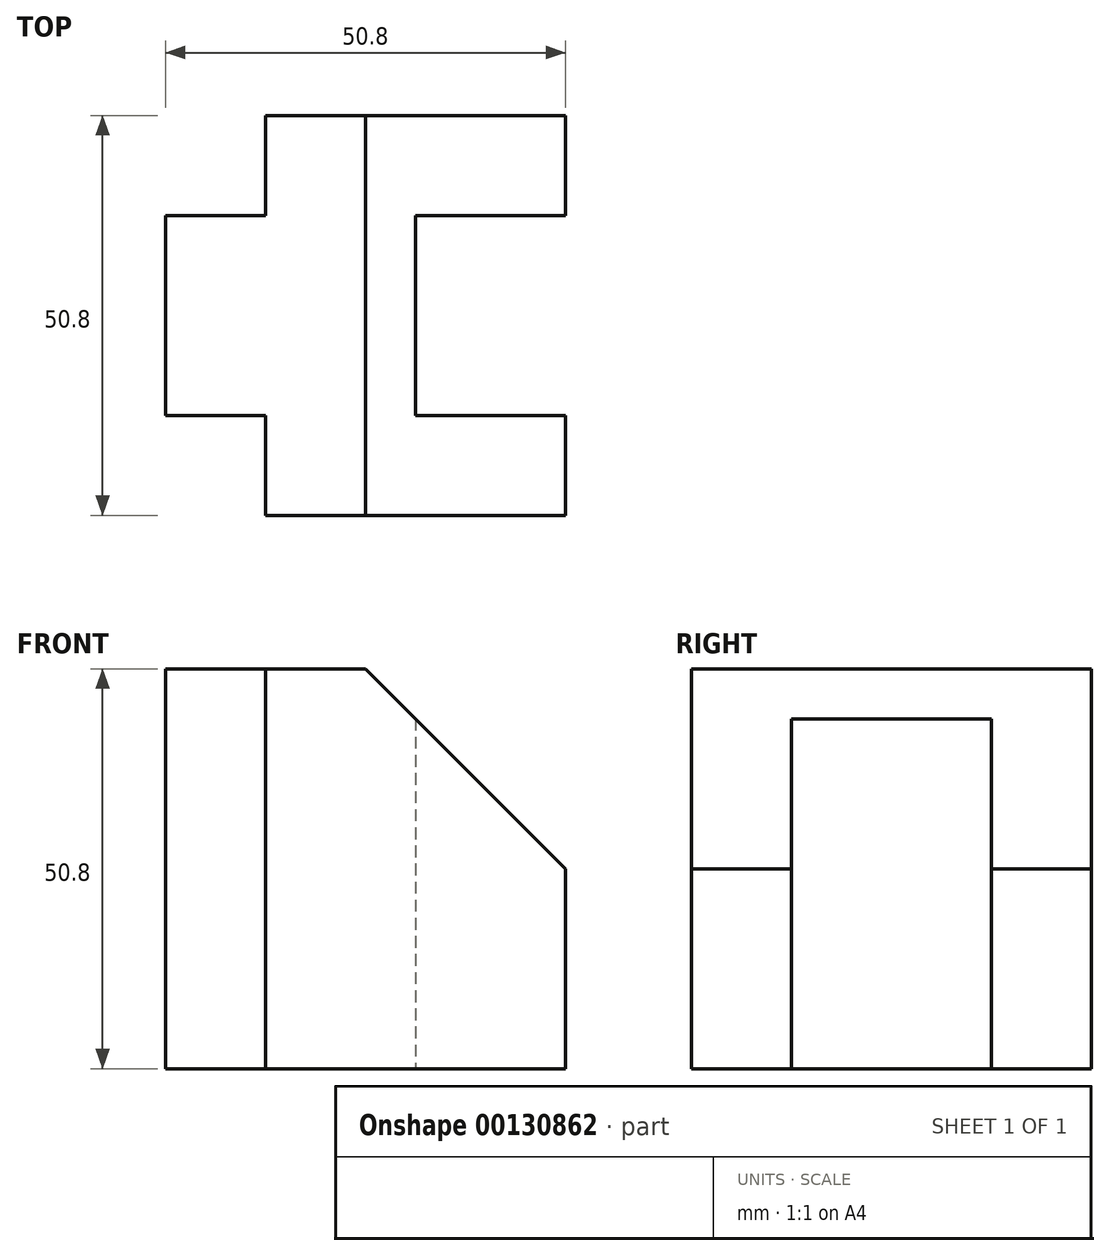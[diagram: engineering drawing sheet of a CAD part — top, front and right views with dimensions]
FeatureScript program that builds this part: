
annotation { "Feature Type Name" : "Feature", "Feature Type Description" : "" }
export const myFeature = defineFeature(function(context is Context, id is Id, definition is map)
    precondition{}
    {
        {
            var Q0;
            Q0=qCreatedBy(makeId("Front.planeOp"),FACE);
            var sketch = newSketch(context, id + "F0", { "sketchPlane" : qUnion([Q0])});
            skLineSegment(sketch, "E0.bottom", {"start": v(0, 0) * mm, "end": v(50.8, 0) * mm});
            skLineSegment(sketch, "E0.top", {"start": v(0, 50.8) * mm, "end": v(25.4, 50.8) * mm});
            skLineSegment(sketch, "E0.left", {"start": v(0, 0) * mm, "end": v(0, 50.8) * mm});
            skLineSegment(sketch, "E0.right", {"start": v(50.8, 0) * mm, "end": v(50.8, 25.4) * mm});
            skLineSegment(sketch, "E1", {"start": v(50.8, 25.4) * mm, "end": v(25.4, 50.8) * mm});
            skLineSegment(sketch, "E2", {"start": v(50.8, 0) * mm, "end": v(50.8, 50.8) * mm, "construction": true});
            skLineSegment(sketch, "E3", {"start": v(50.8, 50.8) * mm, "end": v(0, 50.8) * mm, "construction": true});
            skSolve(sketch);
        }
        {
            var Q0;
            Q0 = qSketchRegion(id + "F0", true);
            extrude(context, id + "F1", {"entities" : qUnion([Q0]), "oppositeDirection" : true, "depth" : 50.8 * mm});
        }
        {
            var Q0;
            Q0=qCreatedBy(makeId("Top.planeOp"),FACE);
            var sketch = newSketch(context, id + "F2", { "sketchPlane" : qUnion([Q0])});
            skLineSegment(sketch, "E4.bottom", {"start": v(0, 0) * mm, "end": v(0, 0) * mm});
            skLineSegment(sketch, "E5.bottom", {"start": v(50.8, 12.7) * mm, "end": v(31.75, 12.7) * mm});
            skLineSegment(sketch, "E5.top", {"start": v(50.8, 38.1) * mm, "end": v(31.75, 38.1) * mm});
            skLineSegment(sketch, "E5.left", {"start": v(50.8, 12.7) * mm, "end": v(50.8, 38.1) * mm});
            skLineSegment(sketch, "E5.right", {"start": v(31.75, 12.7) * mm, "end": v(31.75, 38.1) * mm});
            skLineSegment(sketch, "E6.bottom", {"start": v(0, 38.1) * mm, "end": v(12.7, 38.1) * mm});
            skLineSegment(sketch, "E6.top", {"start": v(0, 50.8) * mm, "end": v(12.7, 50.8) * mm});
            skLineSegment(sketch, "E6.left", {"start": v(0, 38.1) * mm, "end": v(0, 50.8) * mm});
            skLineSegment(sketch, "E6.right", {"start": v(12.7, 38.1) * mm, "end": v(12.7, 50.8) * mm});
            skLineSegment(sketch, "E7.bottom", {"start": v(0, 0) * mm, "end": v(12.7, 0) * mm});
            skLineSegment(sketch, "E7.top", {"start": v(0, 12.7) * mm, "end": v(12.7, 12.7) * mm});
            skLineSegment(sketch, "E7.left", {"start": v(0, 0) * mm, "end": v(0, 12.7) * mm});
            skLineSegment(sketch, "E7.right", {"start": v(12.7, 0) * mm, "end": v(12.7, 12.7) * mm});
            skSolve(sketch);
        }
        {
            var Q0;
            Q0 = qSketchRegion(id + "F2", true);
            extrude(context, id + "F3", {"entities" : qUnion([Q0]), "operationType" : NewBodyOperationType.REMOVE, "endBound" : BoundingType.THROUGH_ALL, "depth" : 25.4 * mm});
        }
    });
